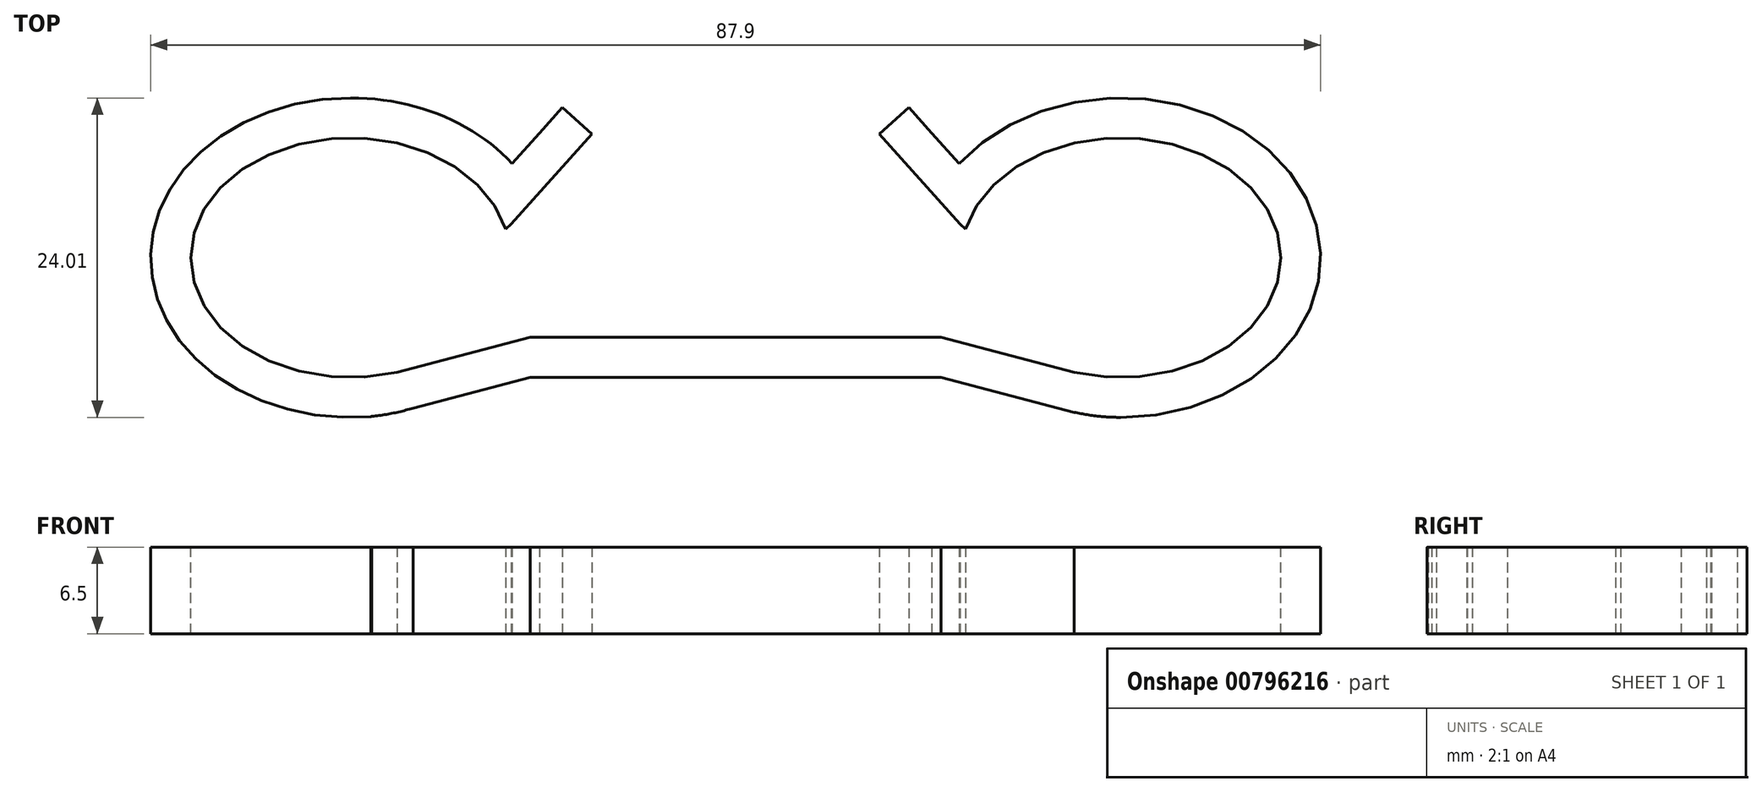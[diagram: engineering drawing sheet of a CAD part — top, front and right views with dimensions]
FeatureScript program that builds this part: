
annotation { "Feature Type Name" : "Feature", "Feature Type Description" : "" }
export const myFeature = defineFeature(function(context is Context, id is Id, definition is map)
    precondition{}
    {
        {
            var Q0;
            Q0=qCreatedBy(makeId("Top.planeOp"),FACE);
            var sketch = newSketch(context, id + "F0", { "sketchPlane" : qUnion([Q0])});
            skLineSegment(sketch, "E0.MirrorCS", {"start": v(0, 0) * mm, "end": v(15.44, 0) * mm});
            skLineSegment(sketch, "E1", {"start": v(-25.44, 0) * mm, "end": v(-25.44, 9) * mm, "construction": true});
            skLineSegment(sketch, "E2.MirrorCS", {"start": v(-25.44, 9) * mm, "end": v(-15.44, 9) * mm, "construction": true});
            skLineSegment(sketch, "E3.MirrorCS", {"start": v(-25.44, 18) * mm, "end": v(-25.44, 9) * mm, "construction": true});
            skLineSegment(sketch, "E4", {"start": v(-15.44, 9) * mm, "end": v(-15.44, 3) * mm, "construction": true});
            skLineSegment(sketch, "E5", {"start": v(-15.44, 9) * mm, "end": v(-16.15, 12.33) * mm, "construction": true});
            skLineSegment(sketch, "E6", {"start": v(-16.15, 12.33) * mm, "end": v(-4.43, 12.33) * mm, "construction": true});
            skLineSegment(sketch, "E7", {"start": v(-16.15, 12.33) * mm, "end": v(-16.15, 23.8) * mm, "construction": true});
            skLineSegment(sketch, "E8", {"start": v(-16.15, 12.33) * mm, "end": v(-14.01, 14.7) * mm});
            skLineSegment(sketch, "E9", {"start": v(0, 0) * mm, "end": v(0, -2.94) * mm, "construction": true});
            skLineSegment(sketch, "E10.MirrorCS", {"start": v(-25.44, 0) * mm, "end": v(-25.44, -2.94) * mm, "construction": true});
            skLineSegment(sketch, "E11", {"start": v(-25.44, 18) * mm, "end": v(-25.44, 21) * mm, "construction": true});
            skEllipticalArc(sketch, "E12", {});
            skLineSegment(sketch, "E13", {"start": v(-14.01, 14.7) * mm, "end": v(-15.86, 17.07) * mm, "construction": true});
            skLineSegment(sketch, "E14", {"start": v(-25.44, 18) * mm, "end": v(-15.86, 18) * mm, "construction": true});
            skLineSegment(sketch, "E15", {"start": v(-10.8, 18.28) * mm, "end": v(-13.03, 20.28) * mm});
            skLineSegment(sketch, "E16", {"start": v(-14.73, 18.35) * mm, "end": v(-13.03, 20.28) * mm});
            skLineSegment(sketch, "E17", {"start": v(-16.15, 12.33) * mm, "end": v(-10.8, 18.28) * mm});
            skLineSegment(sketch, "E18", {"start": v(-15.44, 0) * mm, "end": v(-15.44, 3) * mm, "construction": true});
            skLineSegment(sketch, "E19", {"start": v(-25.44, 0) * mm, "end": v(-25.44, 3) * mm});
            skLineSegment(sketch, "E20", {"start": v(-25.44, 3) * mm, "end": v(-15.44, 3) * mm, "construction": true});
            skLineSegment(sketch, "E21", {"start": v(-15.44, 3) * mm, "end": v(0, 3) * mm});
            skLineSegment(sketch, "E22", {"start": v(-15.44, 0) * mm, "end": v(0, 0) * mm});
            skLineSegment(sketch, "E23.MirrorCS", {"start": v(15.44, 0) * mm, "end": v(15.44, 3) * mm, "construction": true});
            skLineSegment(sketch, "E24.MirrorCS", {"start": v(15.44, 3) * mm, "end": v(0, 3) * mm});
            skEllipticalArc(sketch, "E25.trimOffspring", {});
            skPoint(sketch, "E26.trimOffspring.start.orphan", {"position": v(-38.44, 9) * mm});
            skPoint(sketch, "E27.end.orphan", {"position": v(-35.44, 9) * mm});
            skLineSegment(sketch, "E28", {"start": v(-25.44, 9) * mm, "end": v(-27.44, 9) * mm, "construction": true});
            skLineSegment(sketch, "E29", {"start": v(-27.44, 9) * mm, "end": v(-27.4, -4.8) * mm, "construction": true});
            skLineSegment(sketch, "E30", {"start": v(-27.44, 9) * mm, "end": v(-27.47, 22.4) * mm, "construction": true});
            skLineSegment(sketch, "E31", {"start": v(-25.44, 21) * mm, "end": v(-32.65, 21) * mm, "construction": true});
            skPoint(sketch, "E32", {"position": v(-27.46, 21) * mm});
            skLineSegment(sketch, "E33", {"start": v(-25.44, 18) * mm, "end": v(-36.82, 18) * mm, "construction": true});
            skEllipticalArc(sketch, "E34.trimOffspring", {});
            skLineSegment(sketch, "E35", {"start": v(-16.15, 12.33) * mm, "end": v(-16.86, 11.53) * mm});
            skEllipticalArc(sketch, "E36", {});
            skLineSegment(sketch, "E37", {"start": v(-16.86, 11.53) * mm, "end": v(-16.86, 9) * mm, "construction": true});
            skPoint(sketch, "E38.MirrorCS.end.orphan", {"position": v(10.8, 18.28) * mm});
            skPoint(sketch, "E39.MirrorCS.start.orphan", {"position": v(25.44, 0) * mm});
            skPoint(sketch, "E40.MirrorCS.end.orphan", {"position": v(15.44, 3) * mm});
            skPoint(sketch, "E41.end.orphan", {"position": v(25.44, -2.94) * mm});
            skPoint(sketch, "E42.MirrorCS.end.orphan", {"position": v(15.44, 0) * mm});
            skLineSegment(sketch, "E43", {"start": v(-33.47, 8.99) * mm, "end": v(-38.44, 8.99) * mm, "construction": true});
            skLineSegment(sketch, "E44", {"start": v(-33.47, 8.99) * mm, "end": v(-33.45, -2.01) * mm, "construction": true});
            skEllipticalArc(sketch, "E45", {});
            skEllipticalArc(sketch, "E46.trimOffspring", {});
            skEllipticalArc(sketch, "E47.trimOffspring", {});
            skEllipticalArc(sketch, "E48.trimOffspring", {});
            skLineSegment(sketch, "E49", {"start": v(-16.86, 11.53) * mm, "end": v(-19.56, 11.53) * mm, "construction": true});
            skLineSegment(sketch, "E50", {"start": v(-16.5, 16.57) * mm, "end": v(-14.57, 14.08) * mm, "construction": true});
            skEllipticalArc(sketch, "E51.trimOffspring", {});
            skPoint(sketch, "E52", {"position": v(-18.06, 15.35) * mm});
            skPoint(sketch, "E53.endSnap0", {"position": v(-14.93, 15.88) * mm});
            skPoint(sketch, "E54.MirrorCS.end.orphan", {"position": v(13.03, 20.28) * mm});
            skPoint(sketch, "E54.MirrorCS.start.orphan", {"position": v(15.86, 17.07) * mm});
            skPoint(sketch, "E55.MirrorCS.end.orphan", {"position": v(16.86, 11.53) * mm});
            skPoint(sketch, "E56.MirrorCS.start.orphan", {"position": v(20.28, -1.42) * mm});
            skLineSegment(sketch, "E57.trimOffspring", {"start": v(-14.73, 18.35) * mm, "end": v(-14.93, 18.61) * mm});
            skPoint(sketch, "E58.trimOffspring.end.orphan", {"position": v(-25.13, 0.05) * mm});
            skEllipticalArc(sketch, "E59.trimOffspring", {});
            skPoint(sketch, "E60.start.orphan", {"position": v(-47.78, 8.99) * mm});
            skLineSegment(sketch, "E61", {"start": v(-42.95, 8.99) * mm, "end": v(-43.95, 8.99) * mm, "construction": true});
            skLineSegment(sketch, "E62", {"start": v(-30.46, 18.53) * mm, "end": v(-30.46, 21.53) * mm, "construction": true});
            skPoint(sketch, "E53.end.orphan", {"position": v(-14.53, 18.1) * mm});
            skPoint(sketch, "E53.start.orphan", {"position": v(-13.24, 16.44) * mm});
            skLineSegment(sketch, "E63.trimOffspring", {"start": v(-18.06, 15.35) * mm, "end": v(-19.8, 14) * mm, "construction": true});
            skPoint(sketch, "E64.start.orphan", {"position": v(-15.2, 14.91) * mm});
            skPoint(sketch, "E65.trimOffspring.end.orphan", {"position": v(-24.08, -2.77) * mm});
            skLineSegment(sketch, "E66", {"start": v(-16.15, 12.33) * mm, "end": v(-18.38, 14.33) * mm, "construction": true});
            skLineSegment(sketch, "E67", {"start": v(-14.73, 18.35) * mm, "end": v(-15.94, 17) * mm});
            skLineSegment(sketch, "E68", {"start": v(-19.27, 13.3) * mm, "end": v(-17.6, 10.8) * mm, "construction": true});
            skLineSegment(sketch, "E69.trimOffspring", {"start": v(-16.15, 16.77) * mm, "end": v(-16.8, 16.05) * mm});
            skLineSegment(sketch, "E70", {"start": v(-15.94, 17) * mm, "end": v(-16.15, 16.77) * mm});
            skLineSegment(sketch, "E71", {"start": v(-16.86, 11.53) * mm, "end": v(-17.27, 11.13) * mm});
            skPoint(sketch, "E72.MirrorCS.end.orphan", {"position": v(14.53, 18.1) * mm});
            skPoint(sketch, "E72.MirrorCS.start.orphan", {"position": v(13.24, 16.44) * mm});
            skLineSegment(sketch, "E73.MirrorCS", {"start": v(15.94, 17) * mm, "end": v(16.15, 16.77) * mm});
            skPoint(sketch, "E74.orphan", {"position": v(-17.92, 9) * mm});
            skPoint(sketch, "E75.orphan", {"position": v(17.92, 9) * mm});
            skLineSegment(sketch, "E76", {"start": v(-27.44, 9) * mm, "end": v(-28.94, 9) * mm, "construction": true});
            skLineSegment(sketch, "E77", {"start": v(-38.44, 9) * mm, "end": v(-39.95, 9) * mm, "construction": true});
            skLineSegment(sketch, "E78", {"start": v(-39.95, 9) * mm, "end": v(-40.95, 9) * mm, "construction": true});
            skLineSegment(sketch, "E79", {"start": v(-28.94, 9) * mm, "end": v(-28.94, 18) * mm, "construction": true});
            skEllipticalArc(sketch, "E80", {});
            skPoint(sketch, "E81.center.orphan", {"position": v(-30.46, 9) * mm});
            skPoint(sketch, "E82.orphan", {"position": v(-18.05, 10.35) * mm});
            skLineSegment(sketch, "E83", {"start": v(-40.95, 9) * mm, "end": v(-43.95, 8.99) * mm, "construction": true});
            skLineSegment(sketch, "E84", {"start": v(-28.94, 18) * mm, "end": v(-28.94, 21) * mm, "construction": true});
            skEllipticalArc(sketch, "E85", {});
            skLineSegment(sketch, "E86", {"start": v(-15.44, 0) * mm, "end": v(-22.58, -1.88) * mm});
            skPoint(sketch, "E87.start.orphan", {"position": v(-25.44, -2.87) * mm});
            skPoint(sketch, "E88.end.orphan", {"position": v(-20.28, -1.42) * mm});
            skPoint(sketch, "E89.start.orphan", {"position": v(-25.44, 0.25) * mm});
            skPoint(sketch, "E90.orphan", {"position": v(-22.07, 1) * mm});
            skLineSegment(sketch, "E91", {"start": v(-15.44, 3) * mm, "end": v(-25.44, 0.38) * mm});
            skEllipticalArc(sketch, "E92.trimOffspring", {});
            skPoint(sketch, "E93.MirrorCS.end.orphan", {"position": v(17.23, 15.57) * mm});
            skPoint(sketch, "E93.MirrorCS.start.orphan", {"position": v(25.44, -2.87) * mm});
            skPoint(sketch, "E94.MirrorCS.start.orphan", {"position": v(25.44, 0.25) * mm});
            skPoint(sketch, "E95.MirrorCS.start.orphan", {"position": v(16.15, 12.33) * mm});
            skPoint(sketch, "E96.MirrorCS.end.orphan", {"position": v(15.94, 17) * mm});
            skPoint(sketch, "E96.MirrorCS.start.orphan", {"position": v(14.73, 18.35) * mm});
            skPoint(sketch, "E97.MirrorCS.start.orphan", {"position": v(16.15, 16.77) * mm});
            skPoint(sketch, "E98.MirrorCS.end.orphan", {"position": v(18.05, 10.35) * mm});
            skPoint(sketch, "E99.MirrorCS.end.orphan", {"position": v(22.07, 1) * mm});
            skEllipticalArc(sketch, "E100.MirrorCS", {});
            skLineSegment(sketch, "E101.MirrorCS", {"start": v(15.44, 3) * mm, "end": v(25.44, 0.38) * mm});
            skLineSegment(sketch, "E102.MirrorCS", {"start": v(15.44, 0) * mm, "end": v(25.44, -2.63) * mm});
            skEllipticalArc(sketch, "E103.MirrorCS", {});
            skLineSegment(sketch, "E104.MirrorCS", {"start": v(16.15, 12.33) * mm, "end": v(16.86, 11.53) * mm});
            skLineSegment(sketch, "E105.MirrorCS", {"start": v(16.86, 11.53) * mm, "end": v(17.27, 11.13) * mm});
            skLineSegment(sketch, "E106.MirrorCS", {"start": v(16.15, 12.33) * mm, "end": v(10.8, 18.28) * mm});
            skLineSegment(sketch, "E107.MirrorCS", {"start": v(14.73, 18.35) * mm, "end": v(15.94, 17) * mm});
            skLineSegment(sketch, "E108.MirrorCS", {"start": v(16.15, 16.77) * mm, "end": v(16.8, 16.05) * mm});
            skLineSegment(sketch, "E109.MirrorCS", {"start": v(14.73, 18.35) * mm, "end": v(13.03, 20.28) * mm});
            skLineSegment(sketch, "E110.MirrorCS", {"start": v(10.8, 18.28) * mm, "end": v(13.03, 20.28) * mm});
            skEllipticalArc(sketch, "E111.trimOffspring", {});
            skPoint(sketch, "E112.trimOffspring.start.orphan", {"position": v(-17.22, 15.58) * mm});
            skEllipticalArc(sketch, "E113.trimOffspring", {});
            skEllipticalArc(sketch, "E114.trimOffspring", {});
            skEllipticalArc(sketch, "E115.trimOffspring", {});
            skLineSegment(sketch, "E116", {"start": v(-24.24, -2.31) * mm, "end": v(-22.58, -1.88) * mm});
            skPoint(sketch, "E117.trimOffspring.end.orphan", {"position": v(-25.44, -2.63) * mm});
            skLineSegment(sketch, "E118.trimOffspring", {"start": v(-27.34, -2.93) * mm, "end": v(-27.4, -2.94) * mm});
            skLineSegment(sketch, "E119.trimOffspring", {"start": v(-17.22, 15.58) * mm, "end": v(-17.23, 15.57) * mm});
            skEllipticalArc(sketch, "E120.trimOffspring", {});
            skEllipticalArc(sketch, "E121.MirrorCS", {});
            skEllipticalArc(sketch, "E122.MirrorCS", {});
            skLineSegment(sketch, "E123.MirrorCS", {"start": v(24.24, -2.31) * mm, "end": v(22.58, -1.88) * mm});
            skLineSegment(sketch, "E124.MirrorCS", {"start": v(15.44, 0) * mm, "end": v(22.58, -1.88) * mm});
            skPoint(sketch, "E125.orphan", {"position": v(-16.15, 15.28) * mm});
            skPoint(sketch, "E126.orphan", {"position": v(16.15, 15.28) * mm});
            skLineSegment(sketch, "E127.trimOffspring", {"start": v(17.22, 15.58) * mm, "end": v(17.23, 15.57) * mm});
            const initialGuessF0  = {"E12": [-0.025436057219798212, 0.009, -1, 0, 0.013, 0.011935281218827077, 3.883762500424369, 3.8852733768719823], "E25.trimOffspring": [-0.025436057219798212, 0.009, -1, 0, 0.01, 0.009, 4.910563142848339, 4.9157801796912155], "E34.trimOffspring": [-0.025436057219798212, 0.009, -1, 0, 0.01, 0.009, 1.3714725287653038, 1.3726221643339689], "E36": [-0.027436057219798214, 0.009, -1, 0, 0.014, 0.012124355652985681, 2.6004931276559713, 2.6239055217315177], "E45": [-0.03347489336698898, 0.00898635422016771, -1, 0, 0.014302986616222143, 0.01099998852698997, 4.101996644454546, 4.115540043721714], "E46.trimOffspring": [-0.0274360572198014, 0.009, -1, 0, 0.011, 0.009152553237721217, 0, 0.0014909265790473262], "E47.trimOffspring": [-0.02743605721977554, 0.009, -1, 0, 0.014, 0.012124355652985266, 0, 0.0011254851889609182], "E48.trimOffspring": [-0.02743605721977554, 0.009, -1, 0, 0.014, 0.012124355652985266, 1.1267681756419263, 1.139238243339852], "E51.trimOffspring": [-0.027436057219798218, 0.009, -1, 0, 0.011, 0.009152553237721217, 4.508417403925305, 4.529553843388854], "E59.trimOffspring": [-0.03347489336698898, 0.00898635422016771, -1, 0, 0.014302986616222143, 0.01099998852698997, 1.5725341683452374, 1.583578941095972], "E80": [-0.028936053390229834, 0.008996610502916521, -0.9999999601737223, 0.0002822278405887536, 0.012009789950232322, 0.009003389340031477, 3.3809530069521285, 1.866727825775488], "E85": [-0.028936053390229834, 0.008996610502916521, -0.9999997421754651, -0.0007180870445976052, 0.014012191289206952, 0.012003388673349914, 2.5668347201570287, 2.5750207615117167], "E92.trimOffspring": [-0.028936053390229834, 0.008996610502916521, -0.9999997421754651, -0.0007180870445976052, 0.014012191289206952, 0.012003388673349914, 2.869764099193161, 2.907828436810651], "E100.MirrorCS": [0.028936053390229834, 0.008996610502916521, 0.9999999601737223, 0.0002822278405887536, 0.012009789950232322, 0.009003389340031477, 4.416457481404097, 2.9022323002274577], "E103.MirrorCS": [0.028936061522374833, 0.00899660832032977, 0.9999997421754293, -0.0007180870942184685, 0.014012190309896025, 0.012003388673350124, 4.3710426819269985, 4.71254919457062], "E111.trimOffspring": [-0.02893605436954088, 0.008996610502729397, -0.9999997421754385, -0.0007180870814299518, 0.014012190309896025, 0.012003388673350124, 4.711550719344037, 4.711773769015496], "E113.trimOffspring": [-0.02893605436954088, 0.008996610502729397, -0.9999997421754385, -0.0007180870814299518, 0.014012190309896025, 0.012003388673350124, 6.28281266486746, 0], "E114.trimOffspring": [-0.02893605436954088, 0.008996610502729397, -0.9999997421754385, -0.0007180870814299518, 0.014012190309896025, 0.012003388673350124, 1.6793721734219047, 1.9121420834177945], "E115.trimOffspring": [-0.02893605339023318, 0.008996610502910729, -0.9999997753074361, -0.0006703619002104184, 0.015009762687290347, 0.012003388328433798, 2.6020065178062675, 2.617644658428721], "E120.trimOffspring": [-0.028936053389161016, 0.008996608683919981, -0.9999997753074364, -0.0006703618998398814, 0.015009762687290347, 0.012003388328433798, 3.769232154628477, 1.6721694001179133], "E121.MirrorCS": [0.028936053389161016, 0.008996608683919981, 0.9999997753074364, -0.0006703618998398814, 0.015009762687290347, 0.012003388328433798, 4.611015907061673, 2.5139531525511094], "E122.MirrorCS": [0.02893605436954088, 0.008996610502729397, 0.9999997421754385, -0.0007180870814299518, 0.014012190309896025, 0.012003388673350124, 4.3710432237617916, 4.603813133757681]};
            skSetInitialGuess(sketch, initialGuessF0);
            skSolve(sketch);
        }
        {
            var Q0;
            Q0=makeQuery(id+"F0.imprint","IMPRINT",FACE,{"disambiguationData":[TD([[makeQuery(id+"F0.imprint","IMPRINT",EDGE,{"derivedFrom":sQuery(id+"F0.wireOp",EDGE,"E0.MirrorCS")}),1.0]])]});
            extrude(context, id + "F1", {"entities" : qUnion([Q0]), "depth" : 6.5 * mm, "offsetDistance" : 25 * mm});
        }
    });
